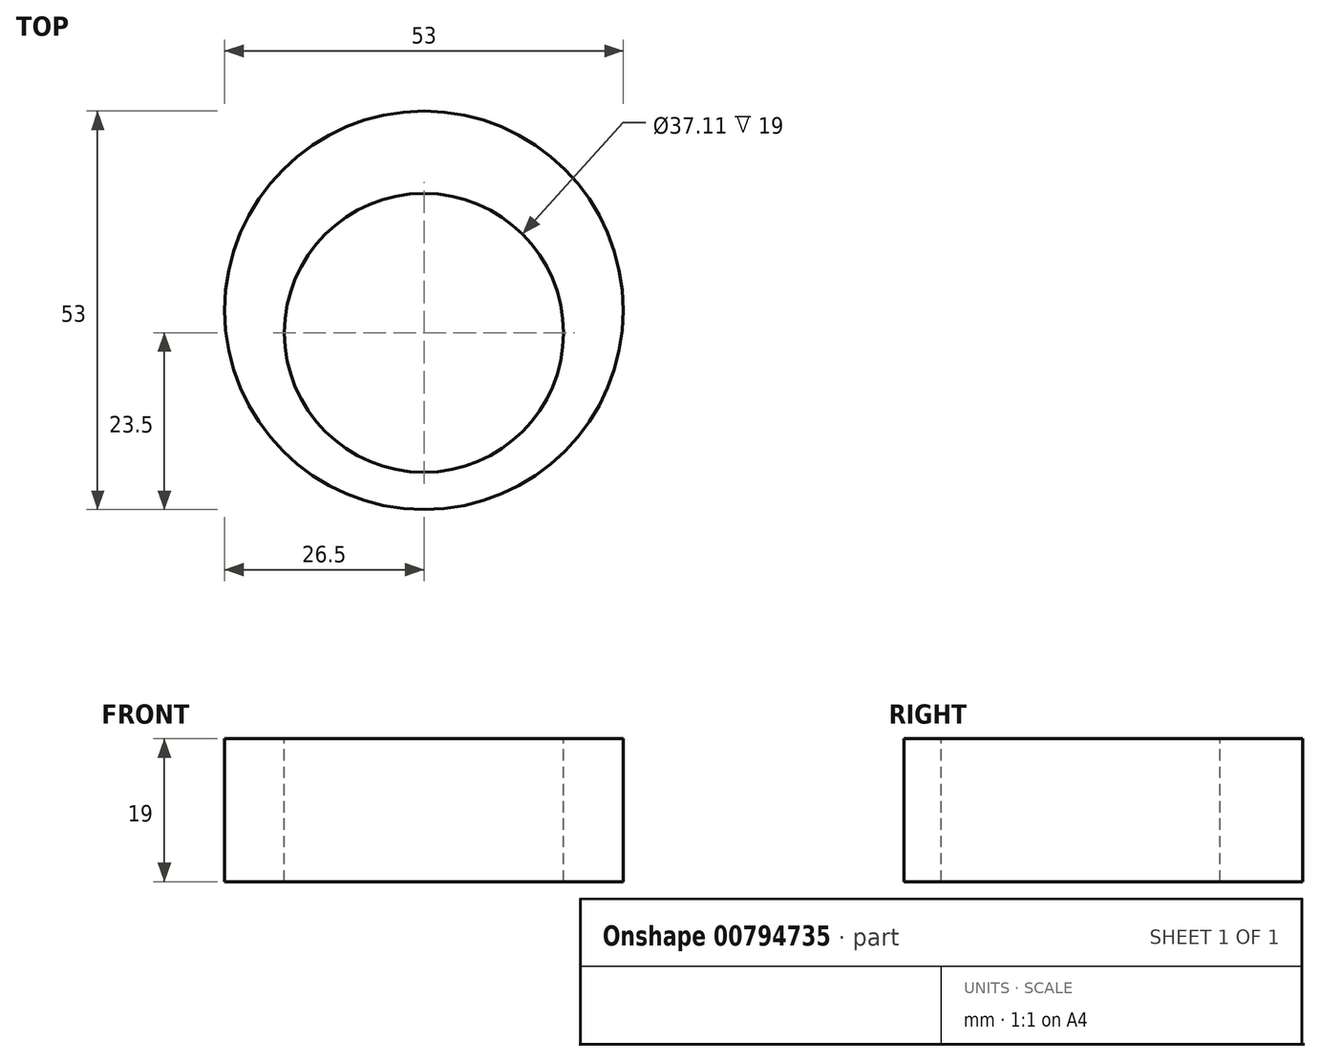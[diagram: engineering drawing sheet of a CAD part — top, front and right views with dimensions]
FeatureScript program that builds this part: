
annotation { "Feature Type Name" : "Feature", "Feature Type Description" : "" }
export const myFeature = defineFeature(function(context is Context, id is Id, definition is map)
    precondition{}
    {
        {
            var Q0;
            Q0=qCreatedBy(makeId("Top.planeOp"),FACE);
            var sketch = newSketch(context, id + "F0", { "sketchPlane" : qUnion([Q0])});
            skCircle(sketch, "E0", {"center": v(0, 0) * mm, "radius": 26.5 * mm});
            skSolve(sketch);
        }
        {
            var Q0;
            Q0 = qSketchRegion(id + "F0", true);
            var Q1;
            Q1=makeQuery(id+"F0.imprint","IMPRINT",FACE,{"disambiguationData":[TD([[makeQuery(id+"F0.imprint","IMPRINT",EDGE,{"derivedFrom":sQuery(id+"F0.wireOp",EDGE,"E0")}),1.0]])]});
            extrude(context, id + "F1", {"entities" : qUnion([Q0, Q1]), "depth" : 19 * mm, "offsetDistance" : 25 * mm});
        }
        {
            var Q0;
            Q0=makeQuery(id+"F1.opExtrude","CAP_FACE",FACE,{"disambiguationData":[OSD([sQuery(id+"F0.wireOp",EDGE,"E0")])],"isStart":false});
            var sketch = newSketch(context, id + "F2", { "sketchPlane" : qUnion([Q0])});
            skCircle(sketch, "E1", {"center": v(0, -3) * mm, "radius": 18.55 * mm});
            skSolve(sketch);
        }
        {
            var Q0;
            Q0 = qSketchRegion(id + "F2", true);
            extrude(context, id + "F3", {"entities" : qUnion([Q0]), "operationType" : NewBodyOperationType.REMOVE, "endBound" : BoundingType.THROUGH_ALL, "oppositeDirection" : true, "depth" : 25 * mm, "offsetDistance" : 25 * mm});
        }
    });
